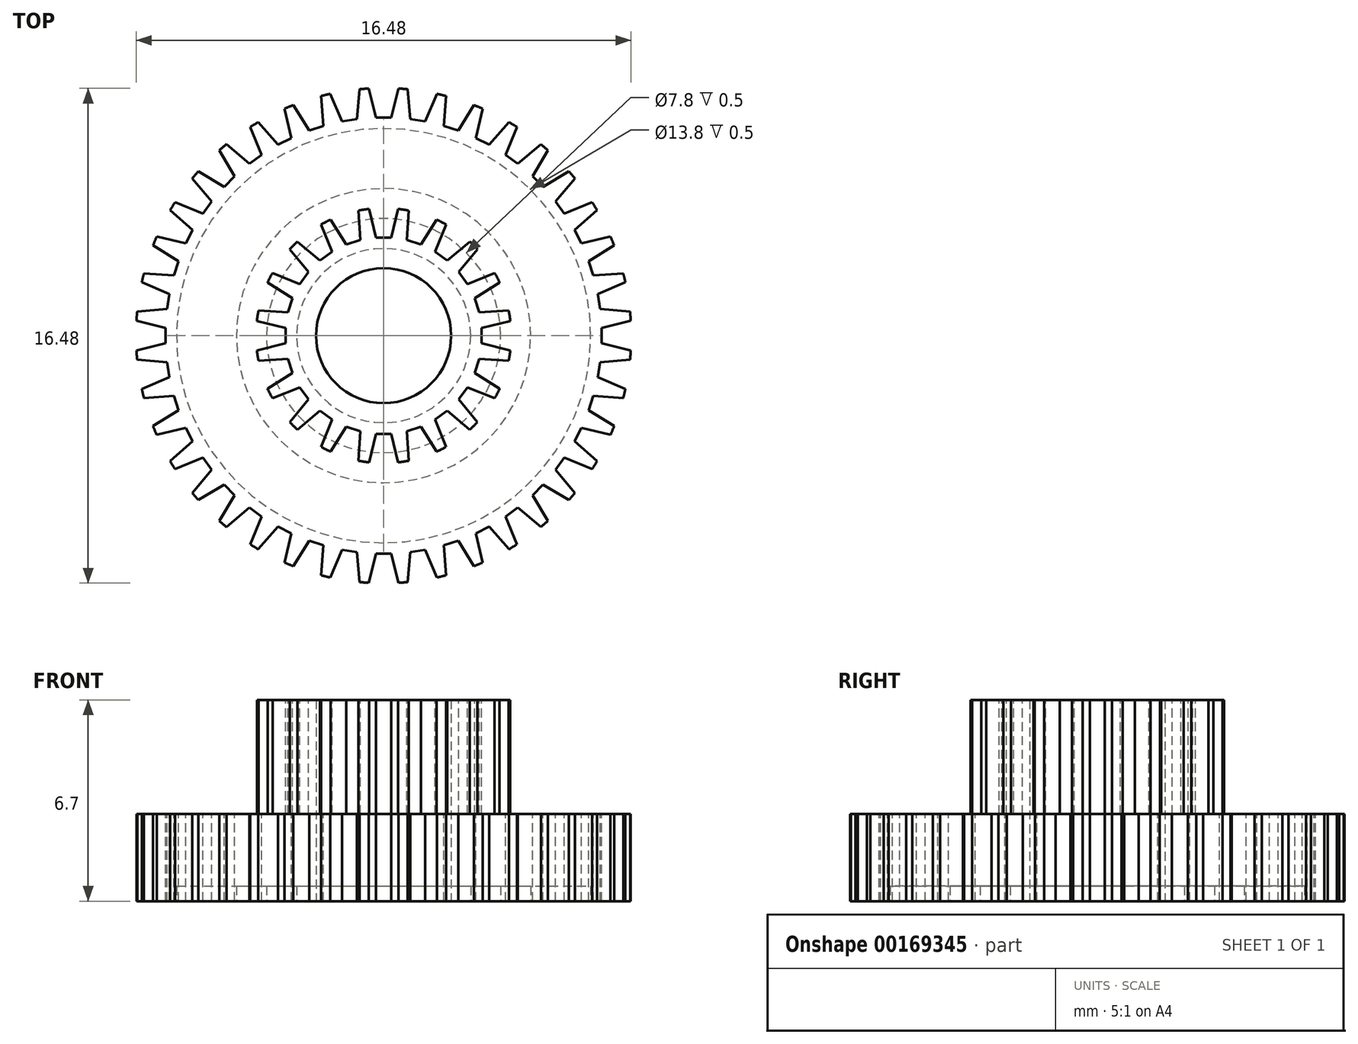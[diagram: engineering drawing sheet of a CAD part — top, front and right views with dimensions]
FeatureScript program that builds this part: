
annotation { "Feature Type Name" : "Feature", "Feature Type Description" : "" }
export const myFeature = defineFeature(function(context is Context, id is Id, definition is map)
    precondition{}
    {
        {
            var Q0;
            Q0=qCreatedBy(makeId("Top.planeOp"),FACE);
            var sketch = newSketch(context, id + "F0", { "sketchPlane" : qUnion([Q0])});
            skCircle(sketch, "E0", {"center": v(0, 0) * mm, "radius": 8.25 * mm});
            skSolve(sketch);
        }
        {
            var Q0;
            Q0=makeQuery(id+"F0.imprint","IMPRINT",FACE,{"disambiguationData":[TD([[makeQuery(id+"F0.imprint","IMPRINT",EDGE,{"derivedFrom":sQuery(id+"F0.wireOp",EDGE,"E0")}),1.0]])]});
            extrude(context, id + "F1", {"entities" : qUnion([Q0]), "depth" : 2.9 * mm});
        }
        {
            var Q0;
            Q0=makeQuery(id+"F1.opExtrude","CAP_FACE",FACE,{"disambiguationData":[OSD([sQuery(id+"F0.wireOp",EDGE,"E0")])],"isStart":false});
            var sketch = newSketch(context, id + "F2", { "sketchPlane" : qUnion([Q0])});
            skCircle(sketch, "E1", {"center": v(0, 0) * mm, "radius": 4.25 * mm});
            skSolve(sketch);
        }
        {
            var Q0;
            Q0=makeQuery(id+"F2.imprint","IMPRINT",FACE,{"disambiguationData":[TD([[makeQuery(id+"F2.imprint","IMPRINT",EDGE,{"derivedFrom":sQuery(id+"F2.wireOp",EDGE,"E1")}),1.0]])]});
            extrude(context, id + "F3", {"entities" : qUnion([Q0]), "operationType" : NewBodyOperationType.ADD, "depth" : 3.8 * mm});
        }
        {
            var Q0;
            Q0=makeQuery(id+"F1.opExtrude","CAP_FACE",FACE,{"disambiguationData":[OSD([sQuery(id+"F0.wireOp",EDGE,"E0")])],"isStart":false});
            var sketch = newSketch(context, id + "F4", { "sketchPlane" : qUnion([Q0])});
            skCircle(sketch, "E2", {"center": v(0, 0) * mm, "radius": 7.27 * mm, "construction": true});
            skLineSegment(sketch, "E3", {"start": v(3.7, 6.26) * mm, "end": v(4.37, 7) * mm, "construction": true});
            skLineSegment(sketch, "E4", {"start": v(-0.5, 8.24) * mm, "end": v(-0.25, 7.27) * mm});
            skLineSegment(sketch, "E5", {"start": v(-0.25, 7.27) * mm, "end": v(0.25, 7.27) * mm});
            skLineSegment(sketch, "E6", {"start": v(0.25, 7.27) * mm, "end": v(0.5, 8.24) * mm});
            skSolve(sketch);
        }
        {
            var Q0;
            {var subQ0=sQuery(id+"F4.wireOp",EDGE,"E4");Q0=makeQuery(id+"F4.imprint","IMPRINT",FACE,{"disambiguationData":[TD([[makeQuery(id+"F4.imprint","IMPRINT",EDGE,{"derivedFrom":subQ0}),1.0]])]});}
            extrude(context, id + "F5", {"entities" : qUnion([Q0]), "operationType" : NewBodyOperationType.REMOVE, "oppositeDirection" : true, "depth" : 2.9 * mm});
        }
        {
            var Q0;
            Q0=makeQuery(id+"F7AvfvGgywbFKeZ_1.opFillet","BLEND_FACE",FACE,{"disambiguationData":[OSD([sQuery(id+"F0.wireOp",EDGE,"E0"),sQuery(id+"F4.wireOp",EDGE,"E6")])]});
            var Q1;
            Q1=makeQuery(id+"F5.boolean.opBoolean","COPY",FACE,{"derivedFrom":makeQuery(id+"F5.opExtrude","SWEPT_FACE",FACE,{"disambiguationData":[OSD([sQuery(id+"F4.wireOp",EDGE,"E6")])]})});
            var Q2;
            Q2=makeQuery(id+"F5.boolean.opBoolean","COPY",FACE,{"derivedFrom":makeQuery(id+"F5.opExtrude","SWEPT_FACE",FACE,{"disambiguationData":[OSD([sQuery(id+"F4.wireOp",EDGE,"E5")])]})});
            var Q3;
            Q3=makeQuery(id+"F5.boolean.opBoolean","COPY",FACE,{"derivedFrom":makeQuery(id+"F5.opExtrude","SWEPT_FACE",FACE,{"disambiguationData":[OSD([sQuery(id+"F4.wireOp",EDGE,"E4")])]})});
            var Q4;
            Q4=makeQuery(id+"F7AvfvGgywbFKeZ_1.opFillet","BLEND_FACE",FACE,{"disambiguationData":[OSD([sQuery(id+"F0.wireOp",EDGE,"E0"),sQuery(id+"F4.wireOp",EDGE,"E4")])]});
            var Q5;
            Q5=makeQuery(id+"F1.opExtrude","SWEPT_FACE",FACE,{"disambiguationData":[OSD([sQuery(id+"F0.wireOp",EDGE,"E0")])]});
            circularPattern(context, id + "F6", {"patternType" : PatternType.FACE, "faces" : qUnion([Q0, Q1, Q2, Q3, Q4]), "axis" : qUnion([Q5]), "angle" : 9 * degree, "instanceCount" : 40});
        }
        {
            var Q0;
            Q0=makeQuery(id+"F3.opExtrude","CAP_FACE",FACE,{"disambiguationData":[OSD([sQuery(id+"F2.wireOp",EDGE,"E1")])],"isStart":false});
            var sketch = newSketch(context, id + "F7", { "sketchPlane" : qUnion([Q0])});
            skCircle(sketch, "E7", {"center": v(0, 0) * mm, "radius": 3.28 * mm, "construction": true});
            skLineSegment(sketch, "E8", {"start": v(1.84, 2.71) * mm, "end": v(2.6, 3.36) * mm, "construction": true});
            skLineSegment(sketch, "E9", {"start": v(-0.49, 4.22) * mm, "end": v(-0.25, 3.27) * mm});
            skLineSegment(sketch, "E10", {"start": v(-0.25, 3.27) * mm, "end": v(0.25, 3.27) * mm});
            skLineSegment(sketch, "E11", {"start": v(0.25, 3.27) * mm, "end": v(0.49, 4.22) * mm});
            skSolve(sketch);
        }
        {
            var Q0;
            {var subQ0=sQuery(id+"F7.wireOp",EDGE,"E9");Q0=makeQuery(id+"F7.imprint","IMPRINT",FACE,{"disambiguationData":[TD([[makeQuery(id+"F7.imprint","IMPRINT",EDGE,{"derivedFrom":subQ0}),1.0]])]});}
            extrude(context, id + "F8", {"entities" : qUnion([Q0]), "operationType" : NewBodyOperationType.REMOVE, "oppositeDirection" : true, "depth" : 3.8 * mm});
        }
        {
            var Q0;
            Q0=makeQuery(id+"F8.boolean.opBoolean","COPY",FACE,{"derivedFrom":makeQuery(id+"F8.opExtrude","SWEPT_FACE",FACE,{"disambiguationData":[OSD([sQuery(id+"F7.wireOp",EDGE,"E9")])]})});
            var Q1;
            Q1=makeQuery(id+"F8.boolean.opBoolean","COPY",FACE,{"derivedFrom":makeQuery(id+"F8.opExtrude","SWEPT_FACE",FACE,{"disambiguationData":[OSD([sQuery(id+"F7.wireOp",EDGE,"E10")])]})});
            var Q2;
            Q2=makeQuery(id+"F8.boolean.opBoolean","COPY",FACE,{"derivedFrom":makeQuery(id+"F8.opExtrude","SWEPT_FACE",FACE,{"disambiguationData":[OSD([sQuery(id+"F7.wireOp",EDGE,"E11")])]})});
            var Q3;
            Q3=makeQuery(id+"F3.opExtrude","SWEPT_FACE",FACE,{"disambiguationData":[OSD([sQuery(id+"F2.wireOp",EDGE,"E1")])]});
            circularPattern(context, id + "F9", {"patternType" : PatternType.FACE, "faces" : qUnion([Q0, Q1, Q2]), "axis" : qUnion([Q3]), "angle" : 18 * degree, "instanceCount" : 20});
        }
        {
            var Q0;
            Q0=makeQuery(id+"F1.opExtrude","CAP_FACE",FACE,{"disambiguationData":[OSD([sQuery(id+"F0.wireOp",EDGE,"E0")])],"isStart":true});
            var sketch = newSketch(context, id + "F10", { "sketchPlane" : qUnion([Q0])});
            skCircle(sketch, "E12", {"center": v(0, 0) * mm, "radius": 2.25 * mm});
            skCircle(sketch, "E13", {"center": v(0, 0) * mm, "radius": 6.9 * mm});
            skCircle(sketch, "E14", {"center": v(0, 0) * mm, "radius": 4.9 * mm});
            skLineSegment(sketch, "E15", {"start": v(0, -4.9) * mm, "end": v(0, -6.9) * mm, "construction": true});
            skCircle(sketch, "E16", {"center": v(0, 0) * mm, "radius": 2.9 * mm});
            skLineSegment(sketch, "E17", {"start": v(0, -2.9) * mm, "end": v(0, -4.9) * mm, "construction": true});
            skCircle(sketch, "E18", {"center": v(0, 0) * mm, "radius": 3.9 * mm});
            skLineSegment(sketch, "E19", {"start": v(0, 2.9) * mm, "end": v(0, 3.9) * mm, "construction": true});
            skSolve(sketch);
        }
        {
            var Q0;
            Q0=makeQuery(id+"F10.imprint","IMPRINT",FACE,{"disambiguationData":[TD([[makeQuery(id+"F10.imprint","IMPRINT",EDGE,{"derivedFrom":sQuery(id+"F10.wireOp",EDGE,"E12")}),1.0]])]});
            extrude(context, id + "F11", {"entities" : qUnion([Q0]), "operationType" : NewBodyOperationType.REMOVE, "oppositeDirection" : true, "depth" : 6.7 * mm});
        }
        {
            var Q0;
            Q0=makeQuery(id+"F10.imprint","IMPRINT",FACE,{"disambiguationData":[TD([[makeQuery(id+"F10.imprint","IMPRINT",EDGE,{"derivedFrom":sQuery(id+"F10.wireOp",EDGE,"E16")}),-1.0]])]});
            var Q1;
            Q1=makeQuery(id+"F10.imprint","IMPRINT",FACE,{"disambiguationData":[TD([[makeQuery(id+"F10.imprint","IMPRINT",EDGE,{"derivedFrom":sQuery(id+"F10.wireOp",EDGE,"E13")}),1.0]])]});
            extrude(context, id + "F12", {"entities" : qUnion([Q0, Q1]), "operationType" : NewBodyOperationType.REMOVE, "oppositeDirection" : true, "depth" : 0.5 * mm});
        }
    });
